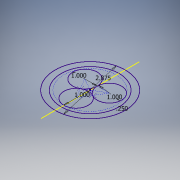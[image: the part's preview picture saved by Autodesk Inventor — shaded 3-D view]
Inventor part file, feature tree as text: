
AUTODESK INVENTOR PART (.ipt)
format: ipt  version: 2018 (Build 220112000, 112)  size: 95,232 bytes
history: native  units: in
note: dims shown in document units (in); Inventor stores cm internally (conversion verified against a paired STEP export)
features: sketch x1
ambient origin geometry x8: Origin, YZ Plane, XZ Plane, XY Plane, X Axis, Y Axis, Z Axis, Center Point
feature tree (1):
  sketch  "Sketch1"  dims[d0=1.0in d1=1.0in d2=1.0in d7=2.875in d8=0.25in]
